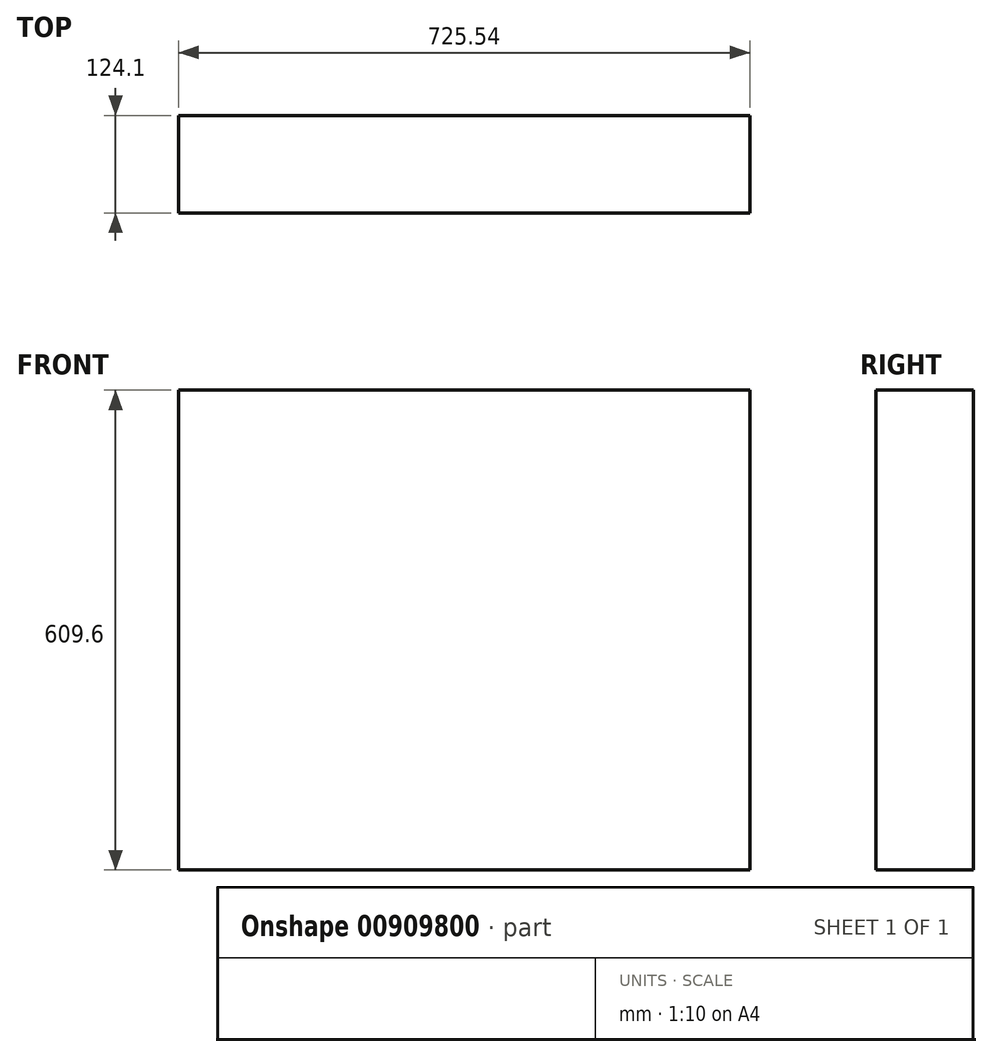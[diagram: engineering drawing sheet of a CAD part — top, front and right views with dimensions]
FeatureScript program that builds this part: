
annotation { "Feature Type Name" : "Feature", "Feature Type Description" : "" }
export const myFeature = defineFeature(function(context is Context, id is Id, definition is map)
    precondition{}
    {
        {
            var Q0;
            Q0=qCreatedBy(makeId("Top.planeOp"),FACE);
            var sketch = newSketch(context, id + "F0", { "sketchPlane" : qUnion([Q0])});
            skPoint(sketch, "E0.middle", {"position": v(0, 0) * mm});
            skLineSegment(sketch, "E1.bottom", {"start": v(362.77, -62.05) * mm, "end": v(-362.77, -62.05) * mm});
            skLineSegment(sketch, "E1.top", {"start": v(362.77, 62.05) * mm, "end": v(-362.77, 62.05) * mm});
            skLineSegment(sketch, "E1.left", {"start": v(362.77, -62.05) * mm, "end": v(362.77, 62.05) * mm});
            skLineSegment(sketch, "E1.right", {"start": v(-362.77, -62.05) * mm, "end": v(-362.77, 62.05) * mm});
            skSolve(sketch);
        }
        {
            var Q0;
            Q0=makeQuery(id+"F0.imprint","IMPRINT",FACE,{"disambiguationData":[TD([[makeQuery(id+"F0.imprint","IMPRINT",EDGE,{"derivedFrom":sQuery(id+"F0.wireOp",EDGE,"E1.bottom")}),-1.0]])]});
            extrude(context, id + "F1", {"entities" : qUnion([Q0]), "depth" : 609.6 * mm, "offsetDistance" : 25.4 * mm});
        }
    });
